# Revit family: レンジフードファン(ブース形自然給気タイプ)2_6
name_source: partatom
category: 機械設備
units: mm (PartAtom-declared; Revit-internal decimal feet)

## family parameters
OmniClass タイトル = Centrifugal Fans
OmniClass 番号 = 23.75.35.17.27
パーツ タイプ = 標準
ロード時にボイドで切り取り = いいえ
丸型コネクタ寸法 = 直径を使用
作業面ベース = いいえ
共有 = いいえ
常に垂直 = はい
部屋計算ポイント = いいえ

## types (5) — shared parameters
D1 = 469
D2 = 480  [stored 1.5748 ft]
D3 = 160  [stored 0.524934 ft]
Depth = 650  [stored 2.13255 ft]
Duct_EA_D = 145  [stored 0.475722 ft]
Duct_EA_H = 91  [stored 0.298556 ft]
Duct_EA_Shutter_Depth = 182  [stored 0.597113 ft]
Duct_EA_Shutter_Height = 182  [stored 0.597113 ft]
Duct_EA_Shutter_Width = 182  [stored 0.597113 ft]
Duct_Height = 55
Duct_SA_D = 365  [stored 1.19751 ft]
Duct_SA_H = 500  [stored 1.64042 ft]
Duct_SA_Pitch = 400  [stored 1.31234 ft]
Duct_SA_Shutter_D = 270  [stored 0.885827 ft]
Duct_SA_Shutter_Height = 190
Duct_SA_Shutter_Width = 560
EAサイズ_D = 148  [stored 0.485564 ft]
EAダクト接続口_上部 = はい
EAダクト接続口_右側面 = いいえ
EAダクト接続口_左側面 = いいえ
EAダクト接続口_後部 = いいえ
H1 = 129  [stored 0.423228 ft]
H2 = 600  [stored 1.9685 ft]
Height = 400  [stored 1.31234 ft]
IfcExportAs = IfcFanType
IfcExportType = CENTRIFUGALFORWARDCURVED
MAX静圧 = 0.0 Pa
MAX風量 = 575.0 m³/h
MID静圧 = 0.0 Pa
MIN静圧 = 0.0 Pa
OmniClassCode = 23-33 31 19 13 15
SAサイズ_D = 148  [stored 0.485564 ft]
SAダクト接続口_右上部 = はい
SAダクト接続口_右側面 = いいえ
SAダクト接続口_右後部 = いいえ
SAダクト接続口_左上部 = いいえ
SAダクト接続口_左側面 = いいえ
SAダクト接続口_左後部 = いいえ
URL = https://www.mitsubishielectric.co.jp
Uniclass2015Code = Pr_65_67_29_12
Uniclass2015Title = Centrifugal fans
Uniclass2015Version = Systems v1.9
☑給気／□排気 = いいえ
ダクト径 = 150 mm
マテリアル = 鋼板(白)
上幕板_右側面 = いいえ
上幕板_左側面 = いいえ
仕様書バージョン = Version1.0
企業コード = 108420
分類コード = 50052503100060
周波数 = 60 Hz
呼称 = 遠心送風機
外気量 = 0.0 m³/h
天吊用穴_D = 255  [stored 0.836614 ft]
天吊用穴_ピッチ = 480  [stored 1.5748 ft]
実風量 = 0.0 m³/h
形式 = 片吸込形
排気量 = 0.0 m³/h
極数 = 2
機外静圧 = 0.0 Pa
機外静圧_排気 = 210.0 Pa
法定耐用年数 = 15
消費電力 = 90 W
相 = 1
積算_科目 = 2 換気設備
符号 = FE
製品リリース年月 = 2022年6月1日
製品出荷対象 = 国内
製造元 = 三菱電機株式会社
設置方法 = 天吊
設計風量 = 0.0 m³/h
説明 = レンジフードファン 深形 自然給気タイプ
負荷分類 = 3_ファン類
運転質量 = 0.00 kg
電動機出力 = 0 W
電圧 = 100 V
風量 = 575.0 m³/h
騒音レベル(dB(A)) = 39
zero-valued in all types: Clearance Back, Clearance Bottom, Clearance Front, Clearance Left, Clearance Right, Clearance Top

## per-type parameters (varying)
| type | MID風量 | MIN風量 | W1 | Width | 価格 | 製品質量 | 質量 |
| V-604KQE9 | 335.0 m³/h | 225.0 m³/h | 300  [stored 0.984252 ft] | 600  [stored 1.9685 ft] | 164000 $ | 21.50 kg | 25.80 kg |
| V-604KQESW8 | 0.0 m³/h | 335.0 m³/h | 300  [stored 0.984252 ft] | 600  [stored 1.9685 ft] | 149100 $ | 21.50 kg | 25.80 kg |
| V-754KQE9 | 335.0 m³/h | 225.0 m³/h | 375  [stored 1.23031 ft] | 750  [stored 2.46063 ft] | 196800 $ | 23.50 kg | 28.20 kg |
| V-754KQESW8 | 335.0 m³/h | 225.0 m³/h | 375  [stored 1.23031 ft] | 750  [stored 2.46063 ft] | 178900 $ | 23.50 kg | 28.20 kg |
| V-904KQE9 | 335.0 m³/h | 225.0 m³/h | 450  [stored 1.47638 ft] | 900  [stored 2.95276 ft] | 231100 $ | 25.50 kg | 30.60 kg |

note: column(s) folded — value = type name in every type: モデル

note: [stored X ft] marks values corroborated as IEEE doubles in the binary element streams (Revit-internal decimal feet)
